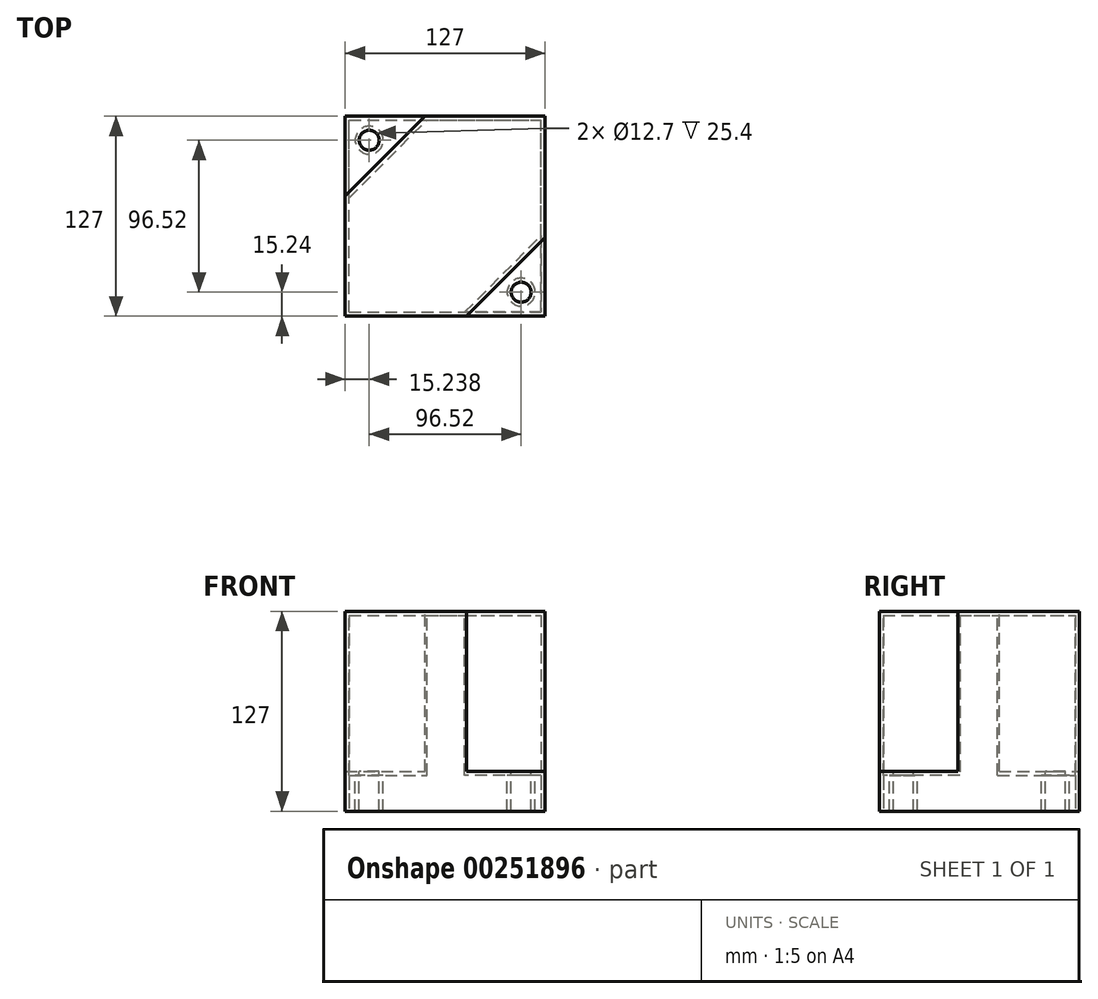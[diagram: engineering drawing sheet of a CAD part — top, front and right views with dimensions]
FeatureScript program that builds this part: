
annotation { "Feature Type Name" : "Feature", "Feature Type Description" : "" }
export const myFeature = defineFeature(function(context is Context, id is Id, definition is map)
    precondition{}
    {
        {
            var Q0;
            Q0=qCreatedBy(makeId("Front.planeOp"),FACE);
            var sketch = newSketch(context, id + "F0", { "sketchPlane" : qUnion([Q0])});
            skLineSegment(sketch, "E0.bottom", {"start": v(-64.72, 61.83) * mm, "end": v(62.28, 61.83) * mm});
            skLineSegment(sketch, "E0.top", {"start": v(-64.72, -65.17) * mm, "end": v(62.28, -65.17) * mm});
            skLineSegment(sketch, "E0.left", {"start": v(-64.72, 61.83) * mm, "end": v(-64.72, -65.17) * mm});
            skLineSegment(sketch, "E0.right", {"start": v(62.28, 61.83) * mm, "end": v(62.28, -65.17) * mm});
            skSolve(sketch);
        }
        {
            var Q0;
            Q0 = qSketchRegion(id + "F0", true);
            extrude(context, id + "F1", {"entities" : qUnion([Q0]), "depth" : 127 * mm});
        }
        {
            var Q0;
            Q0=makeQuery(id+"F1.opExtrude","SWEPT_FACE",FACE,{"disambiguationData":[OSD([sQuery(id+"F0.wireOp",EDGE,"E0.bottom")])]});
            var sketch = newSketch(context, id + "F2", { "sketchPlane" : qUnion([Q0])});
            skLineSegment(sketch, "E1", {"start": v(-64.72, 0) * mm, "end": v(-13.92, 0) * mm});
            skLineSegment(sketch, "E2", {"start": v(-64.72, 0) * mm, "end": v(-64.72, -50.8) * mm});
            skLineSegment(sketch, "E3", {"start": v(-64.72, -50.8) * mm, "end": v(-13.92, 0) * mm});
            skSolve(sketch);
        }
        {
            var Q0;
            {var subQ3=sQuery(id+"F2.wireOp",EDGE,"E3");Q0=makeQuery(id+"F2.imprint","IMPRINT",FACE,{"disambiguationData":[TD([[makeQuery(id+"F2.imprint","IMPRINT",EDGE,{"derivedFrom":subQ3}),-1.0]])]});}
            var sketch = newSketch(context, id + "F3", { "sketchPlane" : qUnion([Q0])});
            skLineSegment(sketch, "E4", {"start": v(62.88, -76.3) * mm, "end": v(62.88, -127.1) * mm});
            skLineSegment(sketch, "E5", {"start": v(62.88, -127.1) * mm, "end": v(12.08, -127.1) * mm});
            skLineSegment(sketch, "E6", {"start": v(12.08, -127.1) * mm, "end": v(62.88, -76.3) * mm});
            skSolve(sketch);
        }
        {
            var Q0;
            Q0 = qSketchRegion(id + "F3", true);
            var Q1;
            Q1 = qSketchRegion(id + "F2", true);
            extrude(context, id + "F4", {"entities" : qUnion([Q0, Q1]), "operationType" : NewBodyOperationType.REMOVE, "oppositeDirection" : true, "depth" : 101.6 * mm});
        }
        {
            var Q0;
            Q0=makeQuery(id+"F4.boolean.opBoolean","COPY",FACE,{"derivedFrom":makeQuery(id+"F4.opExtrude","CAP_FACE",FACE,{"disambiguationData":[OSD([sQuery(id+"F2.wireOp",EDGE,"E1"),sQuery(id+"F2.wireOp",EDGE,"E2"),sQuery(id+"F2.wireOp",EDGE,"E3")])],"isStart":false})});
            var sketch = newSketch(context, id + "F5", { "sketchPlane" : qUnion([Q0])});
            skCircle(sketch, "E7", {"center": v(-49.48, -15.24) * mm, "radius": 6.35 * mm});
            skCircle(sketch, "E8", {"center": v(47.04, -111.76) * mm, "radius": 6.35 * mm});
            skSolve(sketch);
        }
        {
            var Q0;
            Q0 = qSketchRegion(id + "F5", true);
            extrude(context, id + "F6", {"entities" : qUnion([Q0]), "operationType" : NewBodyOperationType.REMOVE, "oppositeDirection" : true, "depth" : 203.2 * mm});
        }
        {
            var Q0;
            Q0=makeQuery(id+"F1.opExtrude","SWEPT_FACE",FACE,{"disambiguationData":[OSD([sQuery(id+"F0.wireOp",EDGE,"E0.top")])]});
            shell(context, id + "F7", {"entities" : qUnion([Q0]), "thickness" : 2.54 * mm});
        }
    });
